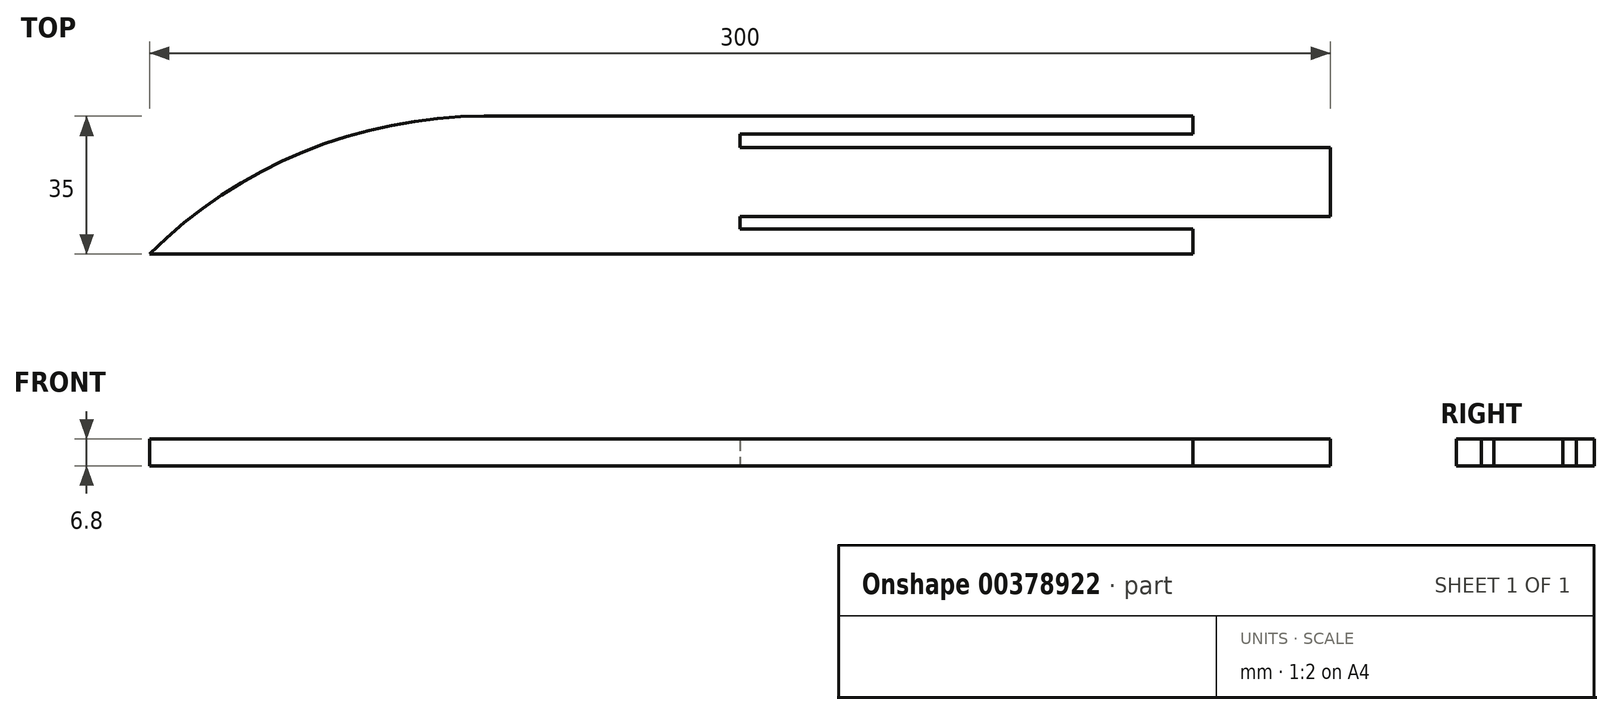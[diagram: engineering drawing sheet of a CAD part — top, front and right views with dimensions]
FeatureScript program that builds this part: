
annotation { "Feature Type Name" : "Feature", "Feature Type Description" : "" }
export const myFeature = defineFeature(function(context is Context, id is Id, definition is map)
    precondition{}
    {
        {
            var Q0;
            Q0=qCreatedBy(makeId("Top.planeOp"),FACE);
            var sketch = newSketch(context, id + "F0", { "sketchPlane" : qUnion([Q0])});
            skLineSegment(sketch, "E0.bottom", {"start": v(-150, 17.5) * mm, "end": v(150, 17.5) * mm});
            skLineSegment(sketch, "E0.top", {"start": v(-150, -17.5) * mm, "end": v(150, -17.5) * mm});
            skLineSegment(sketch, "E0.left", {"start": v(-150, 17.5) * mm, "end": v(-150, -17.5) * mm});
            skLineSegment(sketch, "E0.right", {"start": v(150, 17.5) * mm, "end": v(150, 12.91) * mm});
            skPoint(sketch, "E0.middle", {"position": v(0, 0) * mm});
            skLineSegment(sketch, "E1", {"start": v(0, 12.91) * mm, "end": v(150, 12.91) * mm});
            skLineSegment(sketch, "E2", {"start": v(0, 9.55) * mm, "end": v(150, 9.55) * mm});
            skLineSegment(sketch, "E3", {"start": v(0, 9.55) * mm, "end": v(0, 12.91) * mm});
            skLineSegment(sketch, "E4", {"start": v(0, -11.11) * mm, "end": v(150, -11.11) * mm});
            skLineSegment(sketch, "E5", {"start": v(150, -8.01) * mm, "end": v(0, -8.01) * mm});
            skLineSegment(sketch, "E6", {"start": v(0, -8.01) * mm, "end": v(0, -11.11) * mm});
            skLineSegment(sketch, "E7.trimOffspring", {"start": v(150, -11.11) * mm, "end": v(150, -17.5) * mm});
            skLineSegment(sketch, "E8.trimOffspring", {"start": v(150, 9.55) * mm, "end": v(150, -8.01) * mm});
            skSolve(sketch);
        }
        {
            var Q0;
            Q0=makeQuery(id+"F0.imprint","IMPRINT",FACE,{"disambiguationData":[TD([[makeQuery(id+"F0.imprint","IMPRINT",EDGE,{"derivedFrom":sQuery(id+"F0.wireOp",EDGE,"E0.bottom")}),-1.0]])]});
            extrude(context, id + "F1", {"entities" : qUnion([Q0]), "depth" : 6 * mm});
        }
        {
            var Q0;
            Q0=makeQuery(id+"F1.opExtrude","CAP_FACE",FACE,{"disambiguationData":[OSD([sQuery(id+"F0.wireOp",EDGE,"E0.bottom"),sQuery(id+"F0.wireOp",EDGE,"E0.top"),sQuery(id+"F0.wireOp",EDGE,"E0.left"),sQuery(id+"F0.wireOp",EDGE,"E0.right"),sQuery(id+"F0.wireOp",EDGE,"E1"),sQuery(id+"F0.wireOp",EDGE,"E2"),sQuery(id+"F0.wireOp",EDGE,"E3"),sQuery(id+"F0.wireOp",EDGE,"E4"),sQuery(id+"F0.wireOp",EDGE,"E5"),sQuery(id+"F0.wireOp",EDGE,"E6"),sQuery(id+"F0.wireOp",EDGE,"E7.trimOffspring"),sQuery(id+"F0.wireOp",EDGE,"E8.trimOffspring")])],"isStart":true});
            var Q1;
            Q1=makeQuery(id+"F1.opExtrude","CAP_FACE",FACE,{"disambiguationData":[OSD([sQuery(id+"F0.wireOp",EDGE,"E0.bottom"),sQuery(id+"F0.wireOp",EDGE,"E0.top"),sQuery(id+"F0.wireOp",EDGE,"E0.left"),sQuery(id+"F0.wireOp",EDGE,"E0.right"),sQuery(id+"F0.wireOp",EDGE,"E1"),sQuery(id+"F0.wireOp",EDGE,"E2"),sQuery(id+"F0.wireOp",EDGE,"E3"),sQuery(id+"F0.wireOp",EDGE,"E4"),sQuery(id+"F0.wireOp",EDGE,"E5"),sQuery(id+"F0.wireOp",EDGE,"E6"),sQuery(id+"F0.wireOp",EDGE,"E7.trimOffspring"),sQuery(id+"F0.wireOp",EDGE,"E8.trimOffspring")])],"isStart":false});
            extrude(context, id + "F2", {"entities" : qUnion([Q0, Q1]), "operationType" : NewBodyOperationType.ADD, "depth" : 0.8 * mm});
        }
        {
            var Q0;
            {var subQ0=sQuery(id+"F0.wireOp",EDGE,"E0.left");var subQ1=sQuery(id+"F0.wireOp",EDGE,"E0.bottom");Q0=makeQuery(id+"F2.boolean.opBoolean","MERGE",EDGE,{"derivedFrom":[makeQuery(id+"F1.opExtrude","SWEPT_EDGE",EDGE,{"disambiguationData":[OSD([subQ1,subQ0])]}),makeQuery(id+"F2.opExtrude","SWEPT_EDGE",EDGE,{"disambiguationData":[OSD([subQ1,subQ0]),TDD([makeQuery(id+"F1.opExtrude","CAP_VERTEX",VERTEX,{"disambiguationData":[OSD([subQ1,subQ0])],"isStart":true})])]})]});}
            fillet(context, id + "F3", {"entities" : qUnion([Q0]), "radius" : 120.7 * mm, "tangentPropagation" : true, "allowEdgeOverflow" : false});
        }
        {
            var Q0;
            {var subQ0=sQuery(id+"F0.wireOp",EDGE,"E0.right");Q0=makeQuery(id+"F2.boolean.opBoolean","MERGE",FACE,{"derivedFrom":[makeQuery(id+"F1.opExtrude","SWEPT_FACE",FACE,{"disambiguationData":[OSD([subQ0])]}),makeQuery(id+"F2.opExtrude","SWEPT_FACE",FACE,{"disambiguationData":[OSD([subQ0]),TDD([makeQuery(id+"F1.opExtrude","CAP_EDGE",EDGE,{"disambiguationData":[OSD([subQ0])],"isStart":true})])]})]});}
            var Q1;
            {var subQ0=sQuery(id+"F0.wireOp",EDGE,"E7.trimOffspring");Q1=makeQuery(id+"F2.boolean.opBoolean","MERGE",FACE,{"derivedFrom":[makeQuery(id+"F1.opExtrude","SWEPT_FACE",FACE,{"disambiguationData":[OSD([subQ0])]}),makeQuery(id+"F2.opExtrude","SWEPT_FACE",FACE,{"disambiguationData":[OSD([subQ0]),TDD([makeQuery(id+"F1.opExtrude","CAP_EDGE",EDGE,{"disambiguationData":[OSD([subQ0])],"isStart":true})])]})]});}
            extrude(context, id + "F4", {"entities" : qUnion([Q0, Q1]), "operationType" : NewBodyOperationType.REMOVE, "oppositeDirection" : true, "depth" : 35 * mm});
        }
    });
